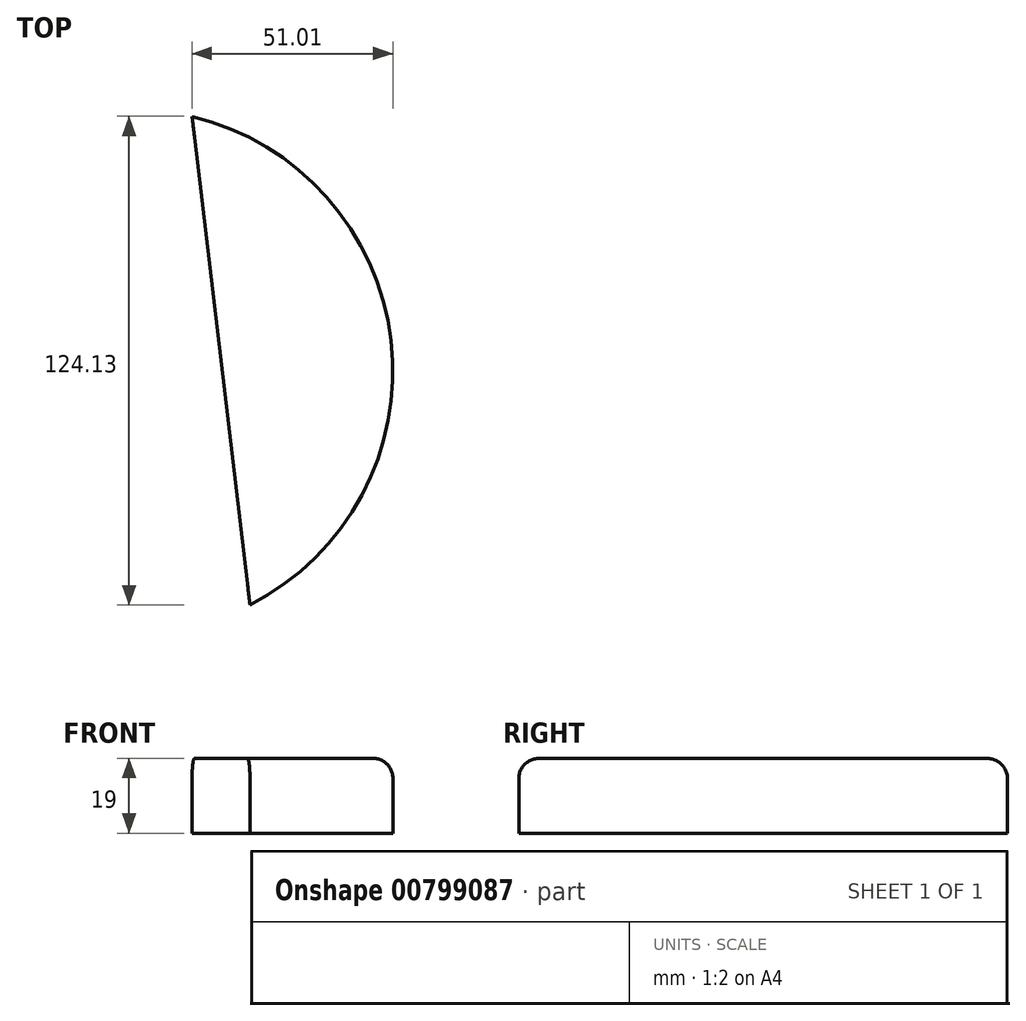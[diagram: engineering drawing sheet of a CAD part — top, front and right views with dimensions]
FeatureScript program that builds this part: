
annotation { "Feature Type Name" : "Feature", "Feature Type Description" : "" }
export const myFeature = defineFeature(function(context is Context, id is Id, definition is map)
    precondition{}
    {
        {
            var Q0;
            Q0=qCreatedBy(makeId("Top.planeOp"),FACE);
            var sketch = newSketch(context, id + "F0", { "sketchPlane" : qUnion([Q0])});
            skLineSegment(sketch, "E0", {"start": v(30.58, -59.32) * mm, "end": v(15.86, 64.8) * mm});
            skArc(sketch, "E1", {"start": v(30.58, -59.32) * mm, "mid": v(66.4, 7.86) * mm, "end": v(15.86, 64.8) * mm});
            skSolve(sketch);
        }
        {
            var Q0;
            Q0 = qSketchRegion(id + "F0", true);
            extrude(context, id + "F1", {"entities" : qUnion([Q0]), "depth" : 19 * mm, "offsetDistance" : 25 * mm});
        }
        {
            var Q0;
            Q0=makeQuery(id+"F1.opExtrude","CAP_EDGE",EDGE,{"disambiguationData":[OSD([sQuery(id+"F0.wireOp",EDGE,"E1")])],"isStart":false});
            fillet(context, id + "F2", {"entities" : qUnion([Q0]), "radius" : 5 * mm, "tangentPropagation" : true, "allowEdgeOverflow" : false});
        }
    });
